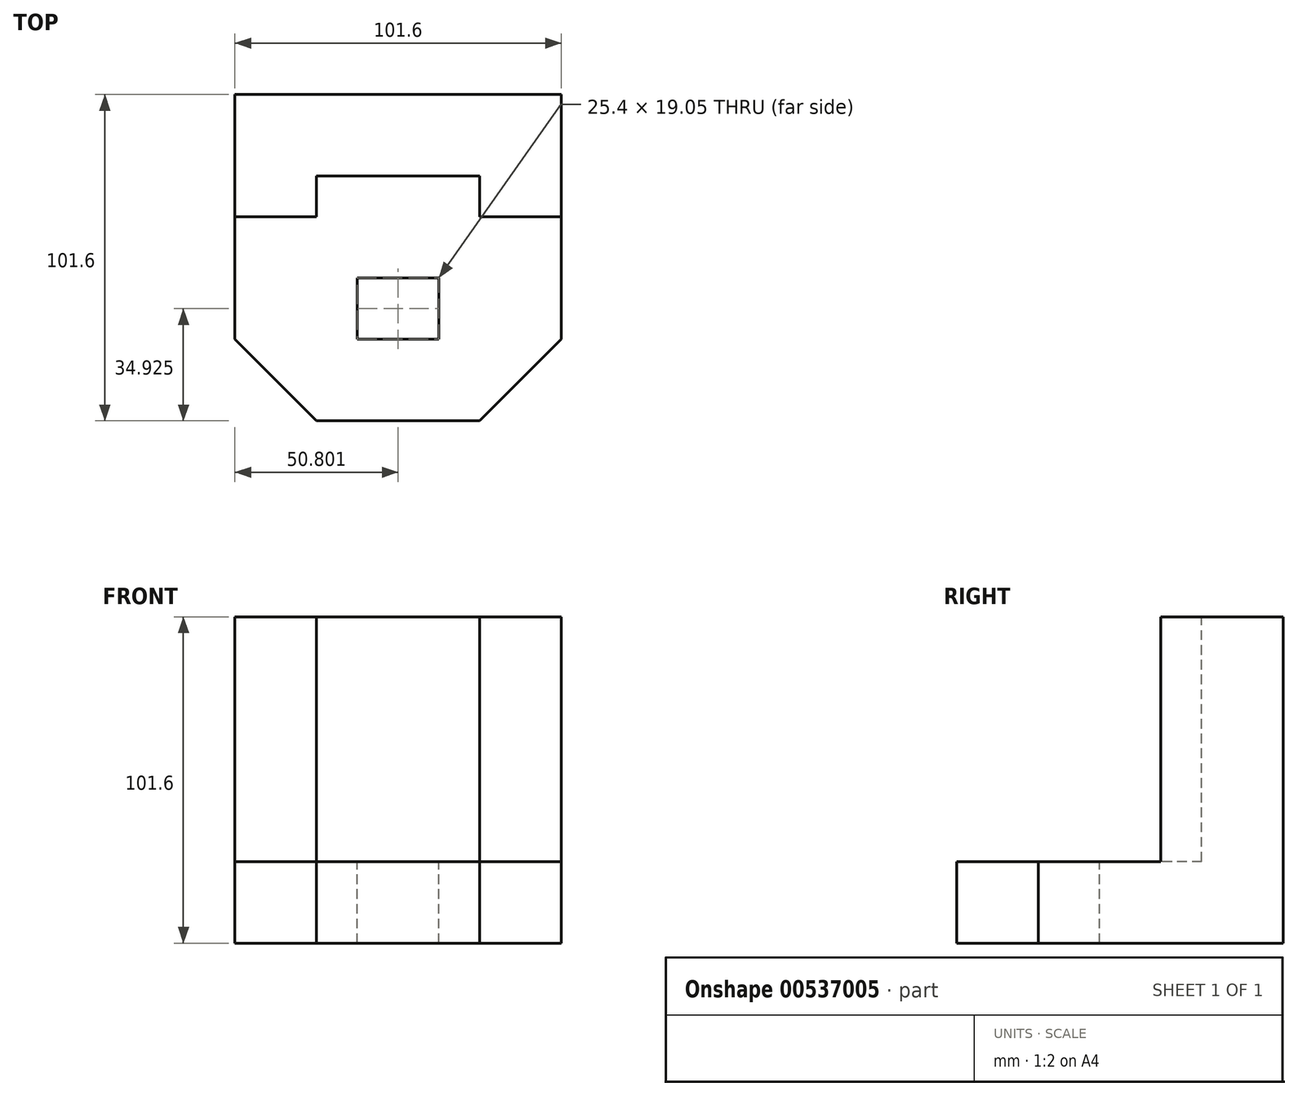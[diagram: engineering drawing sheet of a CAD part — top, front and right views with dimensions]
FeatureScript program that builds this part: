
annotation { "Feature Type Name" : "Feature", "Feature Type Description" : "" }
export const myFeature = defineFeature(function(context is Context, id is Id, definition is map)
    precondition{}
    {
        {
            var Q0;
            Q0=qCreatedBy(makeId("Front.planeOp"),FACE);
            var sketch = newSketch(context, id + "F0", { "sketchPlane" : qUnion([Q0])});
            skLineSegment(sketch, "E0.bottom", {"start": v(-47, -44.76) * mm, "end": v(54.6, -44.76) * mm});
            skLineSegment(sketch, "E0.top", {"start": v(-47, 56.84) * mm, "end": v(54.6, 56.84) * mm});
            skLineSegment(sketch, "E0.left", {"start": v(-47, -44.76) * mm, "end": v(-47, 56.84) * mm});
            skLineSegment(sketch, "E0.right", {"start": v(54.6, -44.76) * mm, "end": v(54.6, 56.84) * mm});
            skSolve(sketch);
        }
        {
            var Q0;
            Q0=makeQuery(id+"F0.imprint","IMPRINT",FACE,{"disambiguationData":[TD([[makeQuery(id+"F0.imprint","IMPRINT",EDGE,{"derivedFrom":sQuery(id+"F0.wireOp",EDGE,"E0.bottom")}),1.0]])]});
            extrude(context, id + "F1", {"entities" : qUnion([Q0]), "depth" : 101.6 * mm, "offsetDistance" : 25.4 * mm});
        }
        {
            var Q0;
            Q0=makeQuery(id+"F1.opExtrude","CAP_FACE",FACE,{"disambiguationData":[OSD([sQuery(id+"F0.wireOp",EDGE,"E0.bottom"),sQuery(id+"F0.wireOp",EDGE,"E0.top"),sQuery(id+"F0.wireOp",EDGE,"E0.left"),sQuery(id+"F0.wireOp",EDGE,"E0.right")])],"isStart":false});
            var sketch = newSketch(context, id + "F2", { "sketchPlane" : qUnion([Q0])});
            skLineSegment(sketch, "E1.bottom", {"start": v(-47, -19.36) * mm, "end": v(-21.6, -19.36) * mm});
            skLineSegment(sketch, "E1.top", {"start": v(-47, 56.84) * mm, "end": v(-21.6, 56.84) * mm});
            skLineSegment(sketch, "E1.left", {"start": v(-47, -19.36) * mm, "end": v(-47, 56.84) * mm});
            skLineSegment(sketch, "E1.right", {"start": v(-21.6, -19.36) * mm, "end": v(-21.6, 56.84) * mm});
            skLineSegment(sketch, "E2.bottom", {"start": v(54.6, -19.36) * mm, "end": v(29.2, -19.36) * mm});
            skLineSegment(sketch, "E2.top", {"start": v(54.6, 56.84) * mm, "end": v(29.2, 56.84) * mm});
            skLineSegment(sketch, "E2.left", {"start": v(54.6, -19.36) * mm, "end": v(54.6, 56.84) * mm});
            skLineSegment(sketch, "E2.right", {"start": v(29.2, -19.36) * mm, "end": v(29.2, 56.84) * mm});
            skLineSegment(sketch, "E3.bottom", {"start": v(-21.6, 56.84) * mm, "end": v(29.2, 56.84) * mm});
            skLineSegment(sketch, "E3.top", {"start": v(-21.6, -19.36) * mm, "end": v(29.2, -19.36) * mm});
            skLineSegment(sketch, "E3.left", {"start": v(-21.6, 56.84) * mm, "end": v(-21.6, -19.36) * mm});
            skLineSegment(sketch, "E3.right", {"start": v(29.2, 56.84) * mm, "end": v(29.2, -19.36) * mm});
            skSolve(sketch);
        }
        {
            var Q0;
            Q0=makeQuery(id+"F2.imprint","IMPRINT",FACE,{"disambiguationData":[TD([[makeQuery(id+"F2.imprint","IMPRINT",EDGE,{"derivedFrom":sQuery(id+"F2.wireOp",EDGE,"E3.bottom")}),-1.0]])]});
            extrude(context, id + "F3", {"entities" : qUnion([Q0]), "operationType" : NewBodyOperationType.REMOVE, "oppositeDirection" : true, "depth" : 76.2 * mm, "offsetDistance" : 25.4 * mm});
        }
        {
            var Q0;
            Q0=makeQuery(id+"F1.opExtrude","CAP_FACE",FACE,{"disambiguationData":[OSD([sQuery(id+"F0.wireOp",EDGE,"E0.bottom"),sQuery(id+"F0.wireOp",EDGE,"E0.top"),sQuery(id+"F0.wireOp",EDGE,"E0.left"),sQuery(id+"F0.wireOp",EDGE,"E0.right")])],"isStart":false});
            var sketch = newSketch(context, id + "F4", { "sketchPlane" : qUnion([Q0])});
            skLineSegment(sketch, "E4.bottom", {"start": v(-21.6, -19.36) * mm, "end": v(-47, -19.36) * mm});
            skLineSegment(sketch, "E4.top", {"start": v(-21.6, 56.84) * mm, "end": v(-47, 56.84) * mm});
            skLineSegment(sketch, "E4.left", {"start": v(-21.6, -19.36) * mm, "end": v(-21.6, 56.84) * mm});
            skLineSegment(sketch, "E4.right", {"start": v(-47, -19.36) * mm, "end": v(-47, 56.84) * mm});
            skLineSegment(sketch, "E5.bottom", {"start": v(29.2, -19.36) * mm, "end": v(54.6, -19.36) * mm});
            skLineSegment(sketch, "E5.top", {"start": v(29.2, 56.84) * mm, "end": v(54.6, 56.84) * mm});
            skLineSegment(sketch, "E5.left", {"start": v(29.2, -19.36) * mm, "end": v(29.2, 56.84) * mm});
            skLineSegment(sketch, "E5.right", {"start": v(54.6, -19.36) * mm, "end": v(54.6, 56.84) * mm});
            skSolve(sketch);
        }
        {
            var Q0;
            Q0=makeQuery(id+"F4.imprint","IMPRINT",FACE,{"disambiguationData":[TD([[makeQuery(id+"F4.imprint","IMPRINT",EDGE,{"derivedFrom":sQuery(id+"F4.wireOp",EDGE,"E5.bottom")}),1.0]])]});
            var Q1;
            Q1=makeQuery(id+"F4.imprint","IMPRINT",FACE,{"disambiguationData":[TD([[makeQuery(id+"F4.imprint","IMPRINT",EDGE,{"derivedFrom":sQuery(id+"F4.wireOp",EDGE,"E4.bottom")}),-1.0]])]});
            extrude(context, id + "F5", {"entities" : qUnion([Q0, Q1]), "operationType" : NewBodyOperationType.REMOVE, "oppositeDirection" : true, "depth" : 63.5 * mm, "offsetDistance" : 25.4 * mm});
        }
        {
            var Q0;
            Q0=makeQuery(id+"F5.boolean.opBoolean","MERGE",FACE,{"derivedFrom":[makeQuery(id+"F3.boolean.opBoolean","COPY",FACE,{"derivedFrom":makeQuery(id+"F3.opExtrude","SWEPT_FACE",FACE,{"disambiguationData":[OSD([sQuery(id+"F2.wireOp",EDGE,"E3.top")])]})}),makeQuery(id+"F5.opExtrude","SWEPT_FACE",FACE,{"disambiguationData":[OSD([sQuery(id+"F4.wireOp",EDGE,"E4.bottom")])]}),makeQuery(id+"F5.opExtrude","SWEPT_FACE",FACE,{"disambiguationData":[OSD([sQuery(id+"F4.wireOp",EDGE,"E5.bottom")])]})]});
            var sketch = newSketch(context, id + "F6", { "sketchPlane" : qUnion([Q0])});
            skLineSegment(sketch, "E6", {"start": v(54.6, -101.6) * mm, "end": v(54.6, -76.2) * mm});
            skLineSegment(sketch, "E7", {"start": v(54.6, -101.6) * mm, "end": v(29.2, -101.6) * mm});
            skLineSegment(sketch, "E8", {"start": v(29.2, -101.6) * mm, "end": v(54.6, -76.2) * mm});
            skSolve(sketch);
        }
        {
            var Q0;
            Q0=qSketchRegion(id+"F6",true);
            extrude(context, id + "F7", {"entities" : qUnion([Q0]), "operationType" : NewBodyOperationType.REMOVE, "oppositeDirection" : true, "depth" : 25.4 * mm, "offsetDistance" : 25.4 * mm});
        }
        {
            var Q0;
            Q0=makeQuery(id+"F5.boolean.opBoolean","MERGE",FACE,{"derivedFrom":[makeQuery(id+"F3.boolean.opBoolean","COPY",FACE,{"derivedFrom":makeQuery(id+"F3.opExtrude","SWEPT_FACE",FACE,{"disambiguationData":[OSD([sQuery(id+"F2.wireOp",EDGE,"E3.top")])]})}),makeQuery(id+"F5.opExtrude","SWEPT_FACE",FACE,{"disambiguationData":[OSD([sQuery(id+"F4.wireOp",EDGE,"E4.bottom")])]}),makeQuery(id+"F5.opExtrude","SWEPT_FACE",FACE,{"disambiguationData":[OSD([sQuery(id+"F4.wireOp",EDGE,"E5.bottom")])]})]});
            var sketch = newSketch(context, id + "F8", { "sketchPlane" : qUnion([Q0])});
            skLineSegment(sketch, "E9", {"start": v(-47, -101.6) * mm, "end": v(-21.6, -101.6) * mm});
            skLineSegment(sketch, "E10", {"start": v(-47, -101.6) * mm, "end": v(-47, -76.2) * mm});
            skLineSegment(sketch, "E11", {"start": v(-47, -76.2) * mm, "end": v(-21.6, -101.6) * mm});
            skSolve(sketch);
        }
        {
            var Q0;
            Q0=makeQuery(id+"F8.imprint","IMPRINT",FACE,{"disambiguationData":[TD([[makeQuery(id+"F8.imprint","IMPRINT",EDGE,{"derivedFrom":sQuery(id+"F8.wireOp",EDGE,"E9")}),1.0]])]});
            extrude(context, id + "F9", {"entities" : qUnion([Q0]), "operationType" : NewBodyOperationType.REMOVE, "oppositeDirection" : true, "depth" : 25.4 * mm, "offsetDistance" : 25.4 * mm});
        }
        {
            var Q0;
            Q0=makeQuery(id+"F5.boolean.opBoolean","MERGE",FACE,{"derivedFrom":[makeQuery(id+"F3.boolean.opBoolean","COPY",FACE,{"derivedFrom":makeQuery(id+"F3.opExtrude","SWEPT_FACE",FACE,{"disambiguationData":[OSD([sQuery(id+"F2.wireOp",EDGE,"E3.top")])]})}),makeQuery(id+"F5.opExtrude","SWEPT_FACE",FACE,{"disambiguationData":[OSD([sQuery(id+"F4.wireOp",EDGE,"E4.bottom")])]}),makeQuery(id+"F5.opExtrude","SWEPT_FACE",FACE,{"disambiguationData":[OSD([sQuery(id+"F4.wireOp",EDGE,"E5.bottom")])]})]});
            var sketch = newSketch(context, id + "F10", { "sketchPlane" : qUnion([Q0])});
            skLineSegment(sketch, "E12", {"start": v(-8.9, -57.15) * mm, "end": v(16.5, -57.15) * mm});
            skPoint(sketch, "E12.endSnap0", {"position": v(54.6, -57.15) * mm});
            skLineSegment(sketch, "E13", {"start": v(-8.9, -57.15) * mm, "end": v(-8.9, -76.2) * mm});
            skLineSegment(sketch, "E14", {"start": v(-8.9, -76.2) * mm, "end": v(16.5, -76.2) * mm});
            skLineSegment(sketch, "E15", {"start": v(16.5, -76.2) * mm, "end": v(16.5, -57.15) * mm});
            skSolve(sketch);
        }
        {
            var Q0;
            Q0=makeQuery(id+"F10.imprint","IMPRINT",FACE,{"disambiguationData":[TD([[makeQuery(id+"F10.imprint","IMPRINT",EDGE,{"derivedFrom":sQuery(id+"F10.wireOp",EDGE,"E12")}),-1.0]])]});
            extrude(context, id + "F11", {"entities" : qUnion([Q0]), "operationType" : NewBodyOperationType.REMOVE, "oppositeDirection" : true, "depth" : 25.4 * mm, "offsetDistance" : 25.4 * mm});
        }
    });
